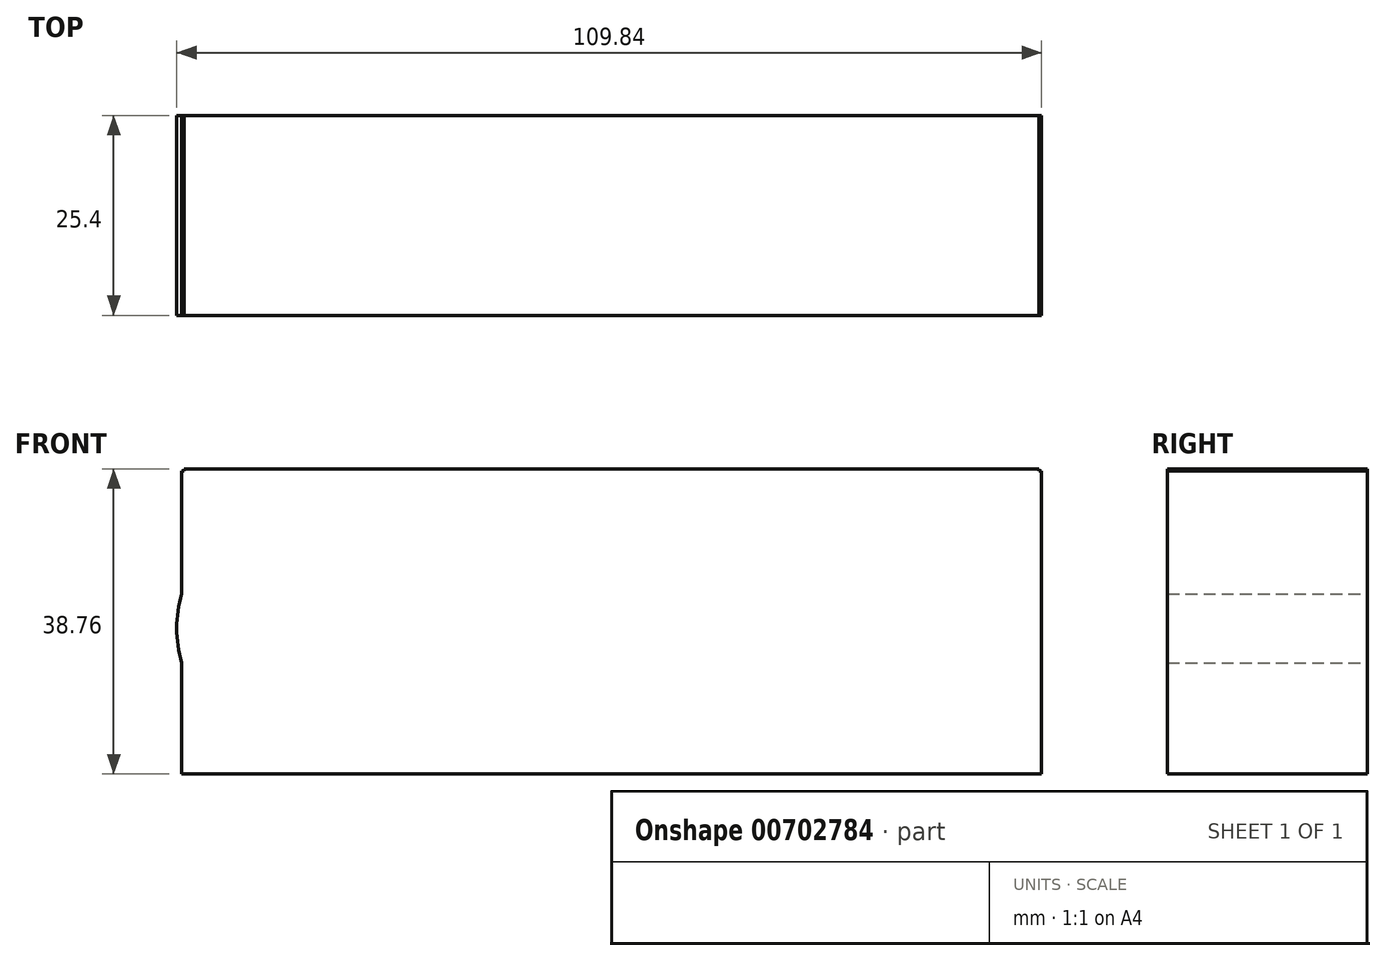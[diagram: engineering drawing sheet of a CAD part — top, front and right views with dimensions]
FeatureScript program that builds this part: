
annotation { "Feature Type Name" : "Feature", "Feature Type Description" : "" }
export const myFeature = defineFeature(function(context is Context, id is Id, definition is map)
    precondition{}
    {
        {
            var Q0;
            Q0=qCreatedBy(makeId("Front.planeOp"),FACE);
            var sketch = newSketch(context, id + "F0", { "sketchPlane" : qUnion([Q0])});
            skLineSegment(sketch, "E0.bottom", {"start": v(-55.35, 41.99) * mm, "end": v(53.88, 41.99) * mm});
            skLineSegment(sketch, "E0.top", {"start": v(-55.35, 3.52) * mm, "end": v(53.88, 3.52) * mm});
            skLineSegment(sketch, "E0.left", {"start": v(-55.35, 41.99) * mm, "end": v(-55.35, 3.52) * mm});
            skLineSegment(sketch, "E0.right", {"start": v(53.88, 41.99) * mm, "end": v(53.88, 3.52) * mm});
            skSolve(sketch);
        }
        {
            var Q0;
            Q0 = qSketchRegion(id + "F0", true);
            extrude(context, id + "F1", {"entities" : qUnion([Q0]), "depth" : 25.4 * mm, "offsetDistance" : 25.4 * mm});
        }
        {
            var Q0;
            Q0=qCreatedBy(makeId("Front.planeOp"),FACE);
            var sketch = newSketch(context, id + "F2", { "sketchPlane" : qUnion([Q0])});
            skLineSegment(sketch, "E1.bottom", {"start": v(-55.05, 42.28) * mm, "end": v(53.58, 42.28) * mm});
            skLineSegment(sketch, "E1.top", {"start": v(-55.05, 3.52) * mm, "end": v(53.58, 3.52) * mm});
            skLineSegment(sketch, "E1.left", {"start": v(-55.05, 42.28) * mm, "end": v(-55.05, 3.52) * mm});
            skLineSegment(sketch, "E1.right", {"start": v(53.58, 42.28) * mm, "end": v(53.58, 3.52) * mm});
            skSolve(sketch);
        }
        {
            var Q0;
            Q0 = qSketchRegion(id + "F2", true);
            extrude(context, id + "F3", {"entities" : qUnion([Q0]), "operationType" : NewBodyOperationType.ADD, "depth" : 25.4 * mm, "offsetDistance" : 25.4 * mm});
        }
        {
            var Q0;
            Q0=qCreatedBy(makeId("Front.planeOp"),FACE);
            var sketch = newSketch(context, id + "F4", { "sketchPlane" : qUnion([Q0])});
            skLineSegment(sketch, "E2", {"start": v(-51.68, 3.6) * mm, "end": v(-51.68, 42) * mm});
            skLineSegment(sketch, "E3", {"start": v(-29.33, 42.7) * mm, "end": v(-29.33, 3.6) * mm});
            skArc(sketch, "E4", {"start": v(-51.68, 32.93) * mm, "mid": v(-39.22, 6.06) * mm, "end": v(-29.33, 33.97) * mm});
            skSolve(sketch);
        }
        {
            var Q0;
            Q0 = qSketchRegion(id + "F4", true);
            extrude(context, id + "F5", {"entities" : qUnion([Q0]), "operationType" : NewBodyOperationType.ADD, "depth" : 25.4 * mm, "offsetDistance" : 25.4 * mm});
        }
    });
